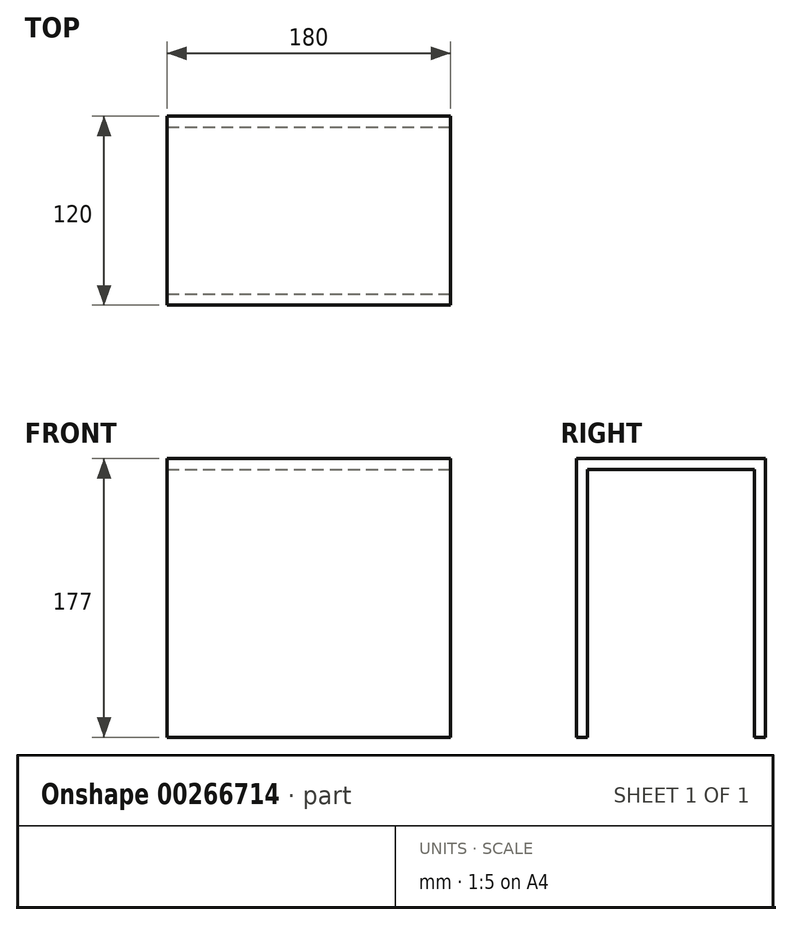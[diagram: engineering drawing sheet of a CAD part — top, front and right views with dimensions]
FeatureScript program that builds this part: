
annotation { "Feature Type Name" : "Feature", "Feature Type Description" : "" }
export const myFeature = defineFeature(function(context is Context, id is Id, definition is map)
    precondition{}
    {
        {
            var Q0;
            Q0=qCreatedBy(makeId("Top.planeOp"),FACE);
            var sketch = newSketch(context, id + "F0", { "sketchPlane" : qUnion([Q0])});
            skLineSegment(sketch, "E0.bottom", {"start": v(-58.5, 73.8) * mm, "end": v(121.5, 73.8) * mm});
            skLineSegment(sketch, "E0.top", {"start": v(-58.5, -46.2) * mm, "end": v(121.5, -46.2) * mm});
            skLineSegment(sketch, "E0.left", {"start": v(-58.5, 73.8) * mm, "end": v(-58.5, -46.2) * mm});
            skLineSegment(sketch, "E0.right", {"start": v(121.5, 73.8) * mm, "end": v(121.5, -46.2) * mm});
            skSolve(sketch);
        }
        {
            var Q0;
            Q0 = qSketchRegion(id + "F0", true);
            extrude(context, id + "F1", {"entities" : qUnion([Q0]), "depth" : 7 * mm});
        }
        {
            var Q0;
            Q0=makeQuery(id+"F1.opExtrude","CAP_FACE",FACE,{"disambiguationData":[OSD([sQuery(id+"F0.wireOp",EDGE,"E0.bottom"),sQuery(id+"F0.wireOp",EDGE,"E0.top"),sQuery(id+"F0.wireOp",EDGE,"E0.left"),sQuery(id+"F0.wireOp",EDGE,"E0.right")])],"isStart":true});
            var sketch = newSketch(context, id + "F2", { "sketchPlane" : qUnion([Q0])});
            skLineSegment(sketch, "E1.bottom", {"start": v(-58.5, -73.8) * mm, "end": v(121.5, -73.8) * mm});
            skLineSegment(sketch, "E1.top", {"start": v(-58.5, -66.8) * mm, "end": v(121.5, -66.8) * mm});
            skLineSegment(sketch, "E1.left", {"start": v(-58.5, -73.8) * mm, "end": v(-58.5, -66.8) * mm});
            skLineSegment(sketch, "E1.right", {"start": v(121.5, -73.8) * mm, "end": v(121.5, -66.8) * mm});
            skSolve(sketch);
        }
        {
            var Q0;
            Q0 = qSketchRegion(id + "F2", true);
            extrude(context, id + "F3", {"entities" : qUnion([Q0]), "operationType" : NewBodyOperationType.ADD, "depth" : 170 * mm});
        }
        {
            var Q0;
            Q0=makeQuery(id+"F1.opExtrude","CAP_FACE",FACE,{"disambiguationData":[OSD([sQuery(id+"F0.wireOp",EDGE,"E0.bottom"),sQuery(id+"F0.wireOp",EDGE,"E0.top"),sQuery(id+"F0.wireOp",EDGE,"E0.left"),sQuery(id+"F0.wireOp",EDGE,"E0.right")])],"isStart":true});
            var sketch = newSketch(context, id + "F4", { "sketchPlane" : qUnion([Q0])});
            skLineSegment(sketch, "E2.bottom", {"start": v(-58.5, 46.2) * mm, "end": v(121.5, 46.2) * mm});
            skLineSegment(sketch, "E2.top", {"start": v(-58.5, 39.2) * mm, "end": v(121.5, 39.2) * mm});
            skLineSegment(sketch, "E2.left", {"start": v(-58.5, 46.2) * mm, "end": v(-58.5, 39.2) * mm});
            skLineSegment(sketch, "E2.right", {"start": v(121.5, 46.2) * mm, "end": v(121.5, 39.2) * mm});
            skSolve(sketch);
        }
        {
            var Q0;
            Q0=makeQuery(id+"F4.imprint","IMPRINT",FACE,{"disambiguationData":[TD([[makeQuery(id+"F4.imprint","IMPRINT",EDGE,{"derivedFrom":sQuery(id+"F4.wireOp",EDGE,"E2.bottom")}),-1.0]])]});
            extrude(context, id + "F5", {"entities" : qUnion([Q0]), "operationType" : NewBodyOperationType.ADD, "depth" : 170 * mm});
        }
    });
